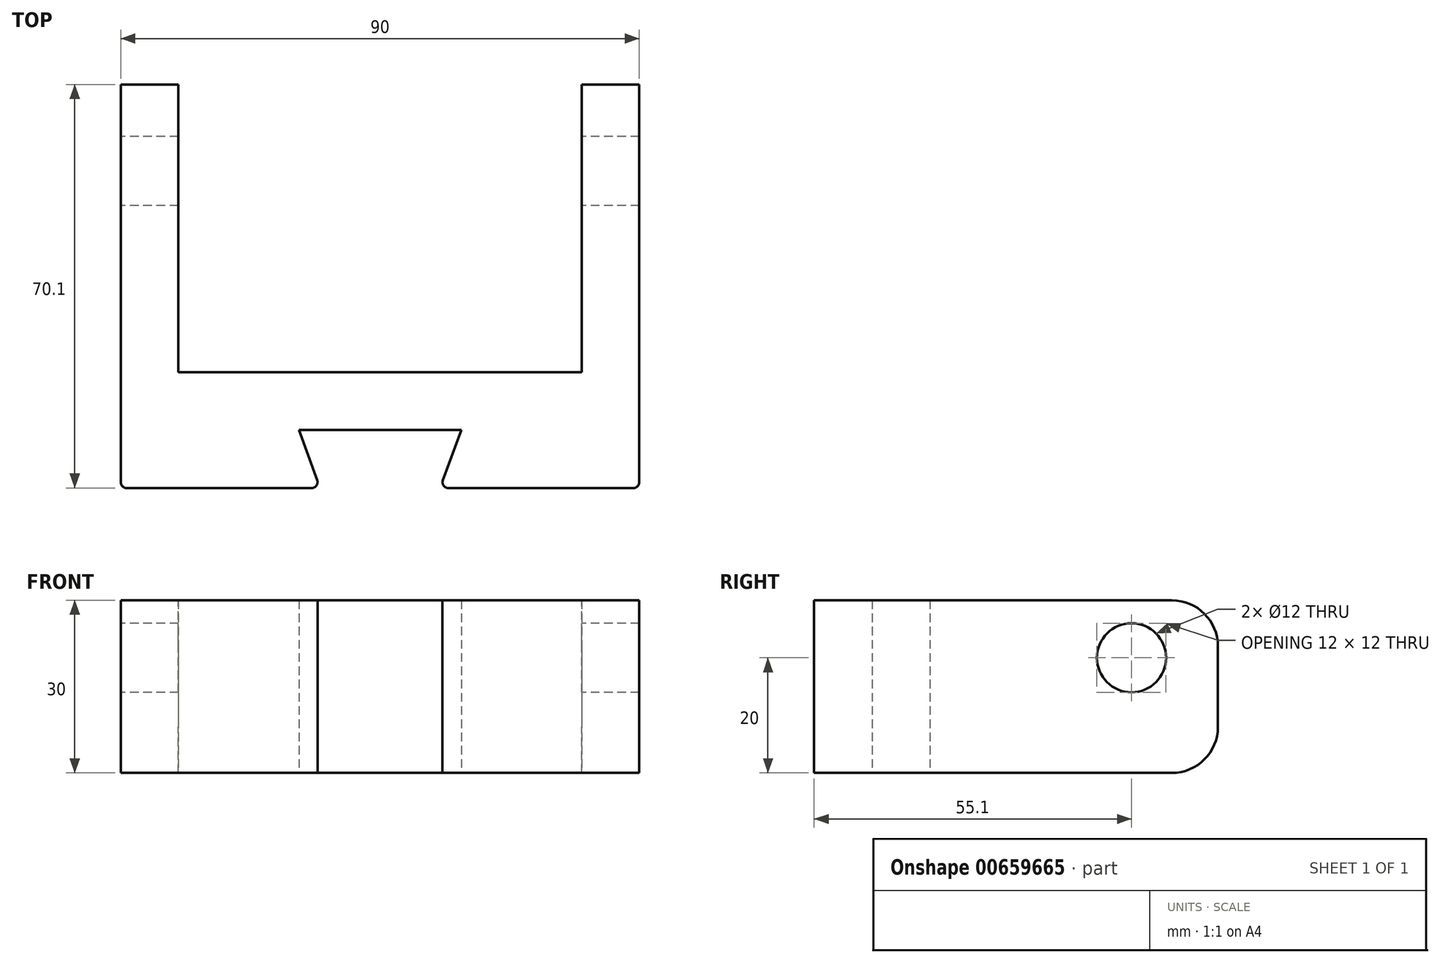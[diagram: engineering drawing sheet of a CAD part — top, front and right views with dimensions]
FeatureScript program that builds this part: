
annotation { "Feature Type Name" : "Feature", "Feature Type Description" : "" }
export const myFeature = defineFeature(function(context is Context, id is Id, definition is map)
    precondition{}
    {
        {
            var Q0;
            Q0=qCreatedBy(makeId("Top.planeOp"),FACE);
            var sketch = newSketch(context, id + "F0", { "sketchPlane" : qUnion([Q0])});
            skLineSegment(sketch, "E0.bottom", {"start": v(-45, 30) * mm, "end": v(45, 30) * mm});
            skLineSegment(sketch, "E0.top", {"start": v(-45, -30) * mm, "end": v(45, -30) * mm});
            skLineSegment(sketch, "E0.left", {"start": v(-45, 30) * mm, "end": v(-45, -30) * mm});
            skLineSegment(sketch, "E0.right", {"start": v(45, 30) * mm, "end": v(45, -30) * mm});
            skPoint(sketch, "E0.middle", {"position": v(0, 0) * mm});
            skLineSegment(sketch, "E1", {"start": v(-45, -30) * mm, "end": v(-45, -40.1) * mm});
            skLineSegment(sketch, "E2", {"start": v(-45, -40.1) * mm, "end": v(-10.42, -40.1) * mm});
            skLineSegment(sketch, "E3", {"start": v(-10.42, -40.1) * mm, "end": v(-14.1, -30) * mm});
            skLineSegment(sketch, "E4", {"start": v(45, -30) * mm, "end": v(45, -40.1) * mm});
            skLineSegment(sketch, "E5", {"start": v(45, -40.1) * mm, "end": v(10.42, -40.1) * mm});
            skLineSegment(sketch, "E6", {"start": v(10.42, -40.1) * mm, "end": v(14.1, -30) * mm});
            skLineSegment(sketch, "E7.bottom", {"start": v(-35, 30) * mm, "end": v(35, 30) * mm});
            skLineSegment(sketch, "E7.top", {"start": v(-35, -20) * mm, "end": v(35, -20) * mm});
            skLineSegment(sketch, "E7.left", {"start": v(-35, 30) * mm, "end": v(-35, -20) * mm});
            skLineSegment(sketch, "E7.right", {"start": v(35, 30) * mm, "end": v(35, -20) * mm});
            skPoint(sketch, "E7.middle", {"position": v(0, 5) * mm});
            skSolve(sketch);
        }
        {
            var Q0;
            {var subQ0=sQuery(id+"F0.wireOp",EDGE,"E1");Q0=makeQuery(id+"F0.imprint","IMPRINT",FACE,{"disambiguationData":[TD([[makeQuery(id+"F0.imprint","IMPRINT",EDGE,{"derivedFrom":subQ0}),1.0]])]});}
            var Q1;
            {var subQ2=sQuery(id+"F0.wireOp",EDGE,"E4");Q1=makeQuery(id+"F0.imprint","IMPRINT",FACE,{"disambiguationData":[TD([[makeQuery(id+"F0.imprint","IMPRINT",EDGE,{"derivedFrom":subQ2}),-1.0]])]});}
            var Q2;
            {var subQ0=sQuery(id+"F0.wireOp",EDGE,"E0.left");Q2=makeQuery(id+"F0.imprint","IMPRINT",FACE,{"disambiguationData":[TD([[makeQuery(id+"F0.imprint","IMPRINT",EDGE,{"derivedFrom":subQ0}),1.0]])]});}
            extrude(context, id + "F1", {"entities" : qUnion([Q0, Q1, Q2]), "depth" : 30 * mm, "offsetDistance" : 25 * mm});
        }
        {
            var Q0;
            Q0=makeQuery(id+"F1.opExtrude","SWEPT_FACE",FACE,{"disambiguationData":[OSD([sQuery(id+"F0.wireOp",EDGE,"E7.right")])]});
            var sketch = newSketch(context, id + "F2", { "sketchPlane" : qUnion([Q0])});
            skCircle(sketch, "E8", {"center": v(-15, 20) * mm, "radius": 6 * mm});
            skSolve(sketch);
        }
        {
            var Q0;
            Q0 = qSketchRegion(id + "F2", true);
            extrude(context, id + "F3", {"entities" : qUnion([Q0]), "operationType" : NewBodyOperationType.REMOVE, "oppositeDirection" : true, "depth" : 10 * mm, "offsetDistance" : 25 * mm, "hasSecondDirection" : true, "secondDirectionOppositeDirection" : false, "secondDirectionDepth" : 80 * mm});
        }
        {
            var Q0;
            {var subQ0=sQuery(id+"F0.wireOp",EDGE,"E0.bottom");Q0=makeQuery(id+"F1.opExtrude","CAP_EDGE",EDGE,{"disambiguationData":[OSD([subQ0]),TDD([makeQuery(id+"F0.imprint","IMPRINT",EDGE,{"disambiguationData":[TD([[makeQuery(id+"F0.imprint","INTERSECT",VERTEX,{"derivedFrom":[subQ0,sQuery(id+"F0.wireOp",EDGE,"E0.right")]}),1.0]])],"derivedFrom":subQ0})])],"isStart":false});}
            var Q1;
            {var subQ0=sQuery(id+"F0.wireOp",EDGE,"E0.bottom");Q1=makeQuery(id+"F1.opExtrude","CAP_EDGE",EDGE,{"disambiguationData":[OSD([subQ0]),TDD([makeQuery(id+"F0.imprint","IMPRINT",EDGE,{"disambiguationData":[TD([[makeQuery(id+"F0.imprint","INTERSECT",VERTEX,{"derivedFrom":[subQ0,sQuery(id+"F0.wireOp",EDGE,"E0.right")]}),1.0]])],"derivedFrom":subQ0})])],"isStart":true});}
            var Q2;
            {var subQ0=sQuery(id+"F0.wireOp",EDGE,"E0.bottom");Q2=makeQuery(id+"F1.opExtrude","CAP_EDGE",EDGE,{"disambiguationData":[OSD([subQ0]),TDD([makeQuery(id+"F0.imprint","IMPRINT",EDGE,{"disambiguationData":[TD([[makeQuery(id+"F0.imprint","INTERSECT",VERTEX,{"derivedFrom":[subQ0,sQuery(id+"F0.wireOp",EDGE,"E7.left")]}),1.0]])],"derivedFrom":subQ0})])],"isStart":false});}
            var Q3;
            {var subQ0=sQuery(id+"F0.wireOp",EDGE,"E0.bottom");Q3=makeQuery(id+"F1.opExtrude","CAP_EDGE",EDGE,{"disambiguationData":[OSD([subQ0]),TDD([makeQuery(id+"F0.imprint","IMPRINT",EDGE,{"disambiguationData":[TD([[makeQuery(id+"F0.imprint","INTERSECT",VERTEX,{"derivedFrom":[subQ0,sQuery(id+"F0.wireOp",EDGE,"E7.left")]}),1.0]])],"derivedFrom":subQ0})])],"isStart":true});}
            fillet(context, id + "F4", {"entities" : qUnion([Q0, Q1, Q2, Q3]), "tangentPropagation" : true, "radius" : 8 * mm, "defaultsChanged" : true, "vertexSettings" : [], "allowEdgeOverflow" : false});
        }
        {
            var Q0;
            Q0=makeQuery(id+"F1.opExtrude","SWEPT_EDGE",EDGE,{"disambiguationData":[OSD([sQuery(id+"F0.wireOp",EDGE,"E2"),sQuery(id+"F0.wireOp",EDGE,"E3")])]});
            var Q1;
            Q1=makeQuery(id+"F1.opExtrude","SWEPT_EDGE",EDGE,{"disambiguationData":[OSD([sQuery(id+"F0.wireOp",EDGE,"E5"),sQuery(id+"F0.wireOp",EDGE,"E6")])]});
            var Q2;
            Q2=makeQuery(id+"F1.opExtrude","SWEPT_EDGE",EDGE,{"disambiguationData":[OSD([sQuery(id+"F0.wireOp",EDGE,"E4"),sQuery(id+"F0.wireOp",EDGE,"E5")])]});
            var Q3;
            Q3=makeQuery(id+"F1.opExtrude","SWEPT_EDGE",EDGE,{"disambiguationData":[OSD([sQuery(id+"F0.wireOp",EDGE,"E1"),sQuery(id+"F0.wireOp",EDGE,"E2")])]});
            fillet(context, id + "F5", {"entities" : qUnion([Q0, Q1, Q2, Q3]), "tangentPropagation" : true, "radius" : 1 * mm, "defaultsChanged" : false, "vertexSettings" : [], "allowEdgeOverflow" : false});
        }
    });
